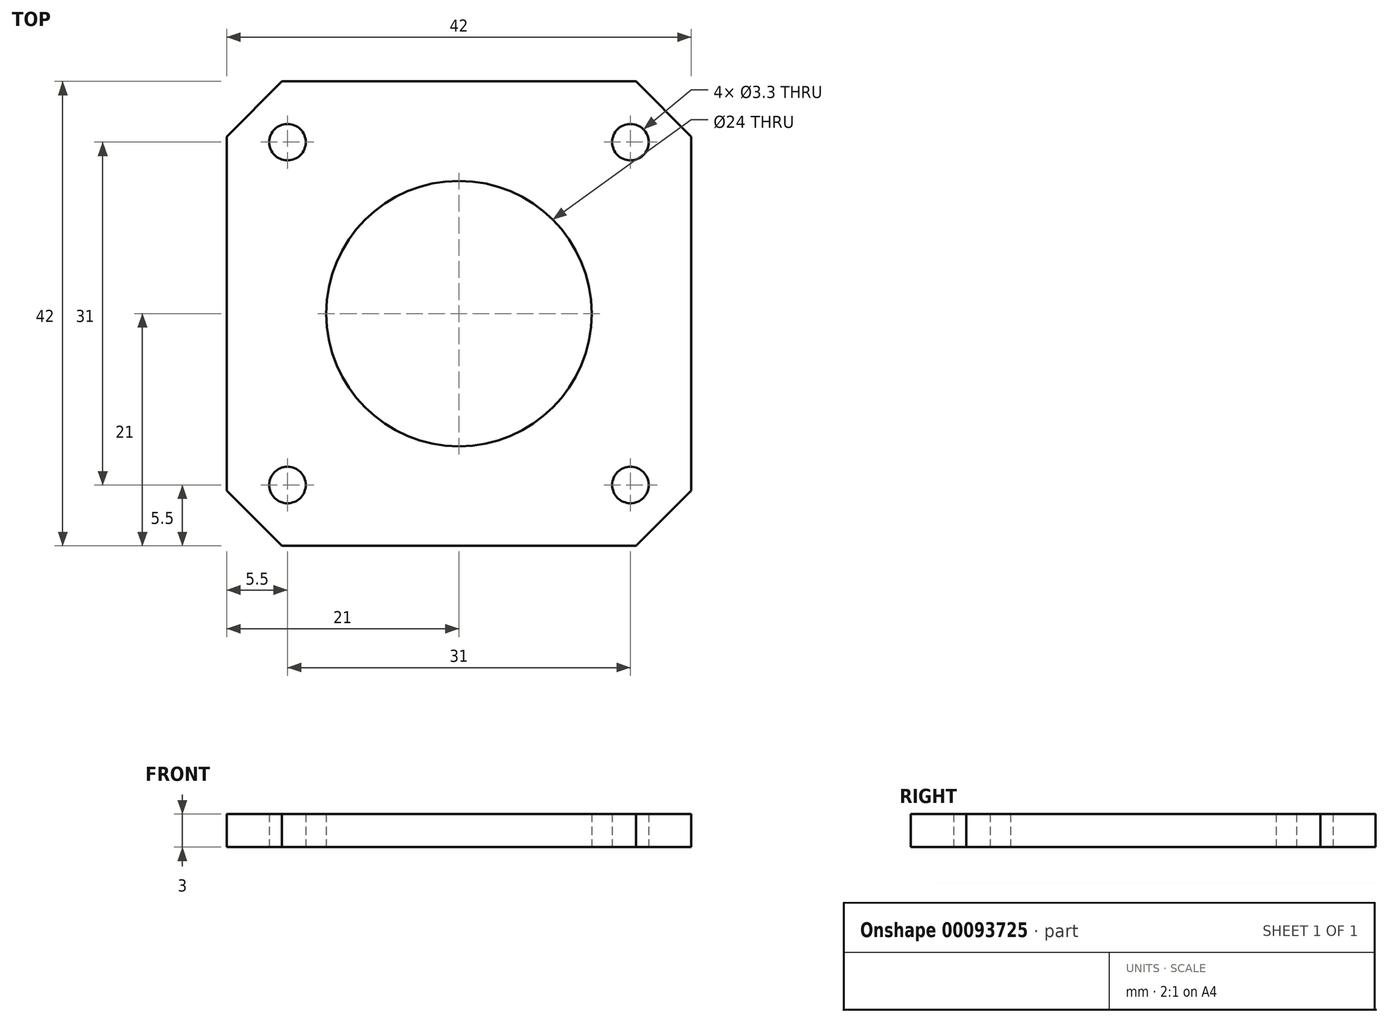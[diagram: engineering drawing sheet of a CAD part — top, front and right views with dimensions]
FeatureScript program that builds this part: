
annotation { "Feature Type Name" : "Feature", "Feature Type Description" : "" }
export const myFeature = defineFeature(function(context is Context, id is Id, definition is map)
    precondition{}
    {
        {
            var Q0;
            Q0=qCreatedBy(makeId("Top.planeOp"),FACE);
            var sketch = newSketch(context, id + "F0", { "sketchPlane" : qUnion([Q0])});
            skLineSegment(sketch, "E0.bottom", {"start": v(-21, 21) * mm, "end": v(21, 21) * mm});
            skLineSegment(sketch, "E0.top", {"start": v(-21, -21) * mm, "end": v(21, -21) * mm});
            skLineSegment(sketch, "E0.left", {"start": v(-21, 21) * mm, "end": v(-21, -21) * mm});
            skLineSegment(sketch, "E0.right", {"start": v(21, 21) * mm, "end": v(21, -21) * mm});
            skPoint(sketch, "E0.middle", {"position": v(0, 0) * mm});
            skCircle(sketch, "E1", {"center": v(-15.5, 15.5) * mm, "radius": 1.65 * mm});
            skCircle(sketch, "E2.MirrorC", {"center": v(15.5, 15.5) * mm, "radius": 1.65 * mm});
            skCircle(sketch, "E3.MirrorC", {"center": v(-15.5, -15.5) * mm, "radius": 1.65 * mm});
            skCircle(sketch, "E4.MirrorC", {"center": v(15.5, -15.5) * mm, "radius": 1.65 * mm});
            skCircle(sketch, "E5", {"center": v(0, 0) * mm, "radius": 12 * mm});
            skSolve(sketch);
        }
        {
            var Q0;
            Q0=makeQuery(id+"F0.imprint","IMPRINT",FACE,{"disambiguationData":[TD([[makeQuery(id+"F0.imprint","IMPRINT",EDGE,{"derivedFrom":sQuery(id+"F0.wireOp",EDGE,"E0.bottom")}),-1.0]])]});
            extrude(context, id + "F1", {"entities" : qUnion([Q0]), "depth" : 3 * mm});
        }
        {
            var Q0;
            Q0=makeQuery(id+"F1.opExtrude","SWEPT_EDGE",EDGE,{"disambiguationData":[OSD([sQuery(id+"F0.wireOp",EDGE,"E0.bottom"),sQuery(id+"F0.wireOp",EDGE,"E0.left")])]});
            var Q1;
            Q1=makeQuery(id+"F1.opExtrude","SWEPT_EDGE",EDGE,{"disambiguationData":[OSD([sQuery(id+"F0.wireOp",EDGE,"E0.top"),sQuery(id+"F0.wireOp",EDGE,"E0.left")])]});
            var Q2;
            Q2=makeQuery(id+"F1.opExtrude","SWEPT_EDGE",EDGE,{"disambiguationData":[OSD([sQuery(id+"F0.wireOp",EDGE,"E0.top"),sQuery(id+"F0.wireOp",EDGE,"E0.right")])]});
            var Q3;
            Q3=makeQuery(id+"F1.opExtrude","SWEPT_EDGE",EDGE,{"disambiguationData":[OSD([sQuery(id+"F0.wireOp",EDGE,"E0.bottom"),sQuery(id+"F0.wireOp",EDGE,"E0.right")])]});
            chamfer(context, id + "F2", {"entities" : qUnion([Q0, Q1, Q2, Q3]), "width" : 5 * mm, "tangentPropagation" : true});
        }
    });
